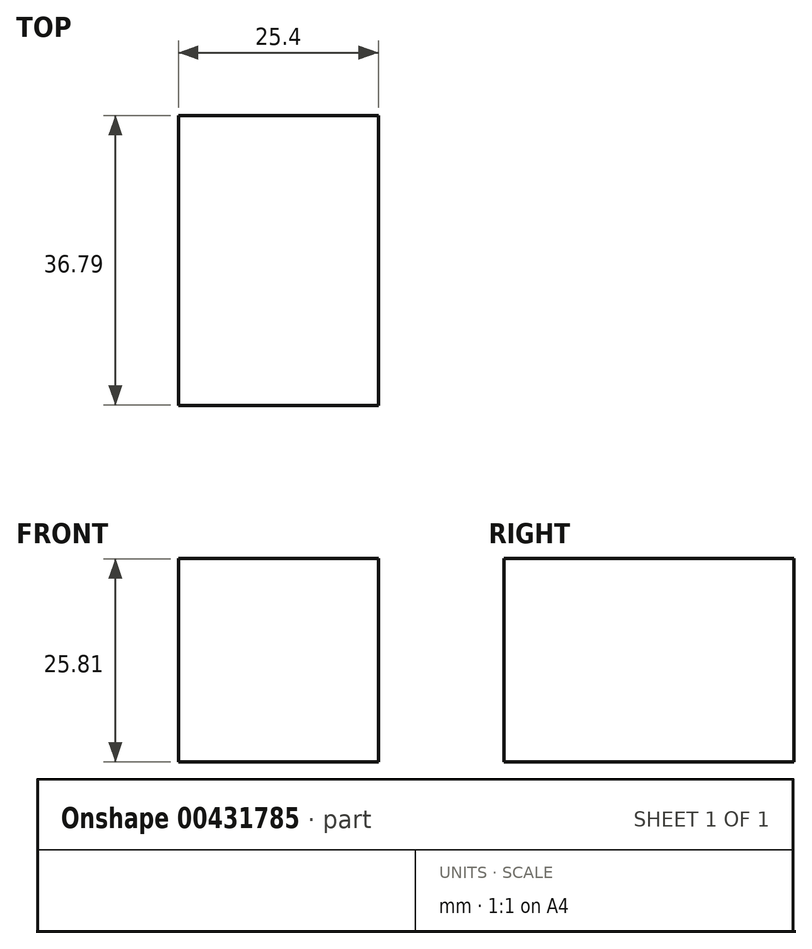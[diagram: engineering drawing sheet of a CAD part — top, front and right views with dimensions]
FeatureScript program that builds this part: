
annotation { "Feature Type Name" : "Feature", "Feature Type Description" : "" }
export const myFeature = defineFeature(function(context is Context, id is Id, definition is map)
    precondition{}
    {
        {
            var Q0;
            Q0=qCreatedBy(makeId("Right.planeOp"),FACE);
            var sketch = newSketch(context, id + "F0", { "sketchPlane" : qUnion([Q0])});
            skLineSegment(sketch, "E0.bottom", {"start": v(-21.96, 25.81) * mm, "end": v(14.83, 25.81) * mm});
            skLineSegment(sketch, "E0.top", {"start": v(-21.96, 0) * mm, "end": v(14.83, 0) * mm});
            skLineSegment(sketch, "E0.left", {"start": v(-21.96, 25.81) * mm, "end": v(-21.96, 0) * mm});
            skLineSegment(sketch, "E0.right", {"start": v(14.83, 25.81) * mm, "end": v(14.83, 0) * mm});
            skSolve(sketch);
        }
        {
            var Q0;
            Q0=makeQuery(id+"F0.imprint","IMPRINT",FACE,{"disambiguationData":[TD([[makeQuery(id+"F0.imprint","IMPRINT",EDGE,{"derivedFrom":sQuery(id+"F0.wireOp",EDGE,"E0.bottom")}),-1.0]])]});
            extrude(context, id + "F1", {"entities" : qUnion([Q0]), "depth" : 25.4 * mm});
        }
    });
